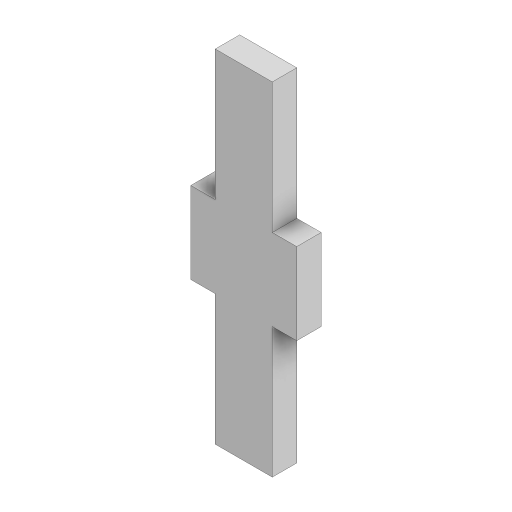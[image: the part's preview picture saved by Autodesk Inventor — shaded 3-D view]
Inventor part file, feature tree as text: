
AUTODESK INVENTOR PART (.ipt)
format: ipt  version: 2023.3 (Build 273359000, 359)  size: 104,960 bytes
history: native  units: mm
features: extrude x1, sketch x1
ambient origin geometry x8: Origin, YZ Plane, XZ Plane, XY Plane, X Axis, Y Axis, Z Axis, Center Point
bodies: Solid1 (feature_tree)
feature tree (2):
  extrude  "Extrusion1"  Depth=13.0mm
  sketch  "Sketch1"  dims[d0=48.0mm d1=13.0mm d2=3.0mm d3=10.0mm d4=7.0mm d5=3.0mm d6=3.0mm d7=0.0mm]
